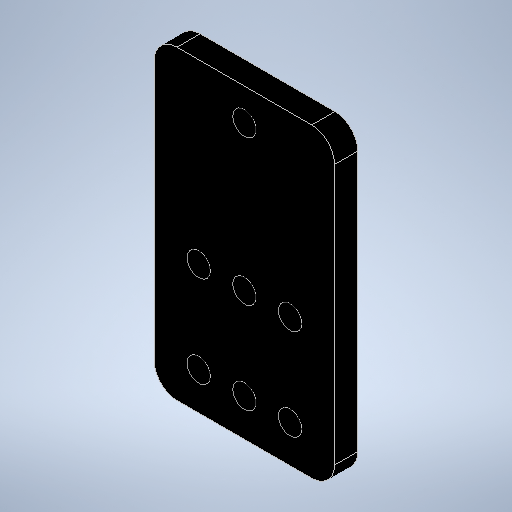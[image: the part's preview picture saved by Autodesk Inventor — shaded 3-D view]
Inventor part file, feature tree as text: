
AUTODESK INVENTOR PART (.ipt)
format: ipt  version: 2025.1 (Build 291241020, 241B)  size: 267,776 bytes
history: native  units: in
note: dims shown in document units (in); Inventor stores cm internally (conversion verified against a paired STEP export)
features: extrude x1, sketch x1, projected_geometry x1, other x1
ambient origin geometry x8: Origin, YZ Plane, XZ Plane, XY Plane, X Axis, Y Axis, Z Axis, Center Point
bodies: Solid1 (feature_tree)
feature tree (4):
  extrude  "Extrusion1"  [1 undecoded]
  sketch  "Sketch1"  dims[d0=0.0827in d1=0.0in]
  projected_geometry  "Projected Loop1"
  other  "Boss-Extrude1"
note: 1 required parameter value undecoded (feature->parameter linkage not recoverable at this tier; creation-order binding heuristic only, values carry confidence <= 0.55)
